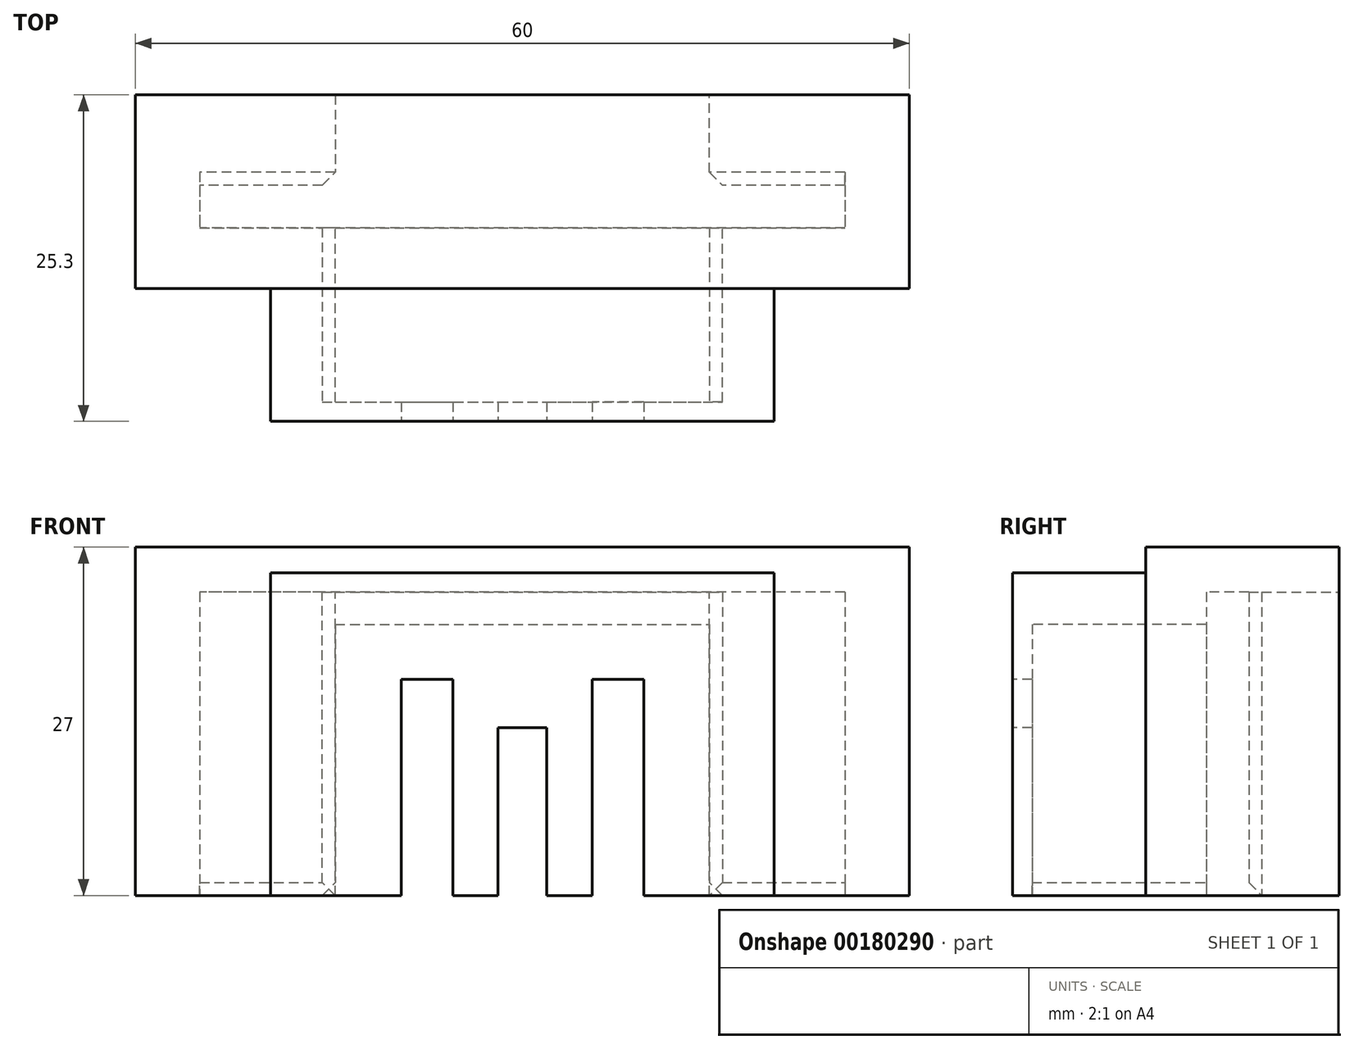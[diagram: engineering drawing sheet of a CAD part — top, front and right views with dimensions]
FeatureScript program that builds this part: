
annotation { "Feature Type Name" : "Feature", "Feature Type Description" : "" }
export const myFeature = defineFeature(function(context is Context, id is Id, definition is map)
    precondition{}
    {
        {
            var Q0;
            Q0=qCreatedBy(makeId("Front.planeOp"),FACE);
            var sketch = newSketch(context, id + "F0", { "sketchPlane" : qUnion([Q0])});
            skLineSegment(sketch, "E0", {"start": v(14.25, 0) * mm, "end": v(14.25, 21) * mm, "construction": true});
            skPoint(sketch, "E1.visualSharp", {"position": v(0, 0) * mm});
            skLineSegment(sketch, "E2.6", {"start": v(-0.25, 21) * mm, "end": v(28.75, 21) * mm});
            skLineSegment(sketch, "E3", {"start": v(-0.25, 21) * mm, "end": v(-0.25, 0) * mm});
            skLineSegment(sketch, "E4", {"start": v(28.75, 21) * mm, "end": v(28.75, 0) * mm});
            skLineSegment(sketch, "E5.0", {"start": v(-3.25, 23.75) * mm, "end": v(-3.25, 0) * mm});
            skLineSegment(sketch, "E5.4", {"start": v(-3.25, 23.75) * mm, "end": v(31.75, 23.75) * mm});
            skLineSegment(sketch, "E5.5", {"start": v(31.75, 23.75) * mm, "end": v(31.75, 0) * mm});
            skLineSegment(sketch, "E6", {"start": v(-3.25, 0) * mm, "end": v(-0.25, 0) * mm});
            skLineSegment(sketch, "E7", {"start": v(28.75, 0) * mm, "end": v(31.75, 0) * mm});
            skLineSegment(sketch, "E8", {"start": v(-0.25, 0) * mm, "end": v(28.75, 0) * mm, "construction": true});
            skSolve(sketch);
        }
        {
            var Q0;
            Q0=qSketchRegion(id+"F0",true);
            extrude(context, id + "F1", {"entities" : qUnion([Q0]), "oppositeDirection" : true, "depth" : 15.8 * mm});
        }
        {
            var Q0;
            Q0=makeQuery(id+"F1.opExtrude","CAP_FACE",FACE,{"disambiguationData":[OSD([sQuery(id+"F0.wireOp",EDGE,"E2.0"),sQuery(id+"F0.wireOp",EDGE,"E2.1"),sQuery(id+"F0.wireOp",EDGE,"E2.2"),sQuery(id+"F0.wireOp",EDGE,"E2.3"),sQuery(id+"F0.wireOp",EDGE,"E2.4"),sQuery(id+"F0.wireOp",EDGE,"E2.5"),sQuery(id+"F0.wireOp",EDGE,"E2.6"),sQuery(id+"F0.wireOp",EDGE,"E3"),sQuery(id+"F0.wireOp",EDGE,"E4"),sQuery(id+"F0.wireOp",EDGE,"E5.0"),sQuery(id+"F0.wireOp",EDGE,"E5.1"),sQuery(id+"F0.wireOp",EDGE,"E5.2"),sQuery(id+"F0.wireOp",EDGE,"E5.3"),sQuery(id+"F0.wireOp",EDGE,"E5.4"),sQuery(id+"F0.wireOp",EDGE,"E5.5"),sQuery(id+"F0.wireOp",EDGE,"E5.6"),sQuery(id+"F0.wireOp",EDGE,"E5.7"),sQuery(id+"F0.wireOp",EDGE,"E5.8"),sQuery(id+"F0.wireOp",EDGE,"E6"),sQuery(id+"F0.wireOp",EDGE,"E7")])],"isStart":true});
            var sketch = newSketch(context, id + "F2", { "sketchPlane" : qUnion([Q0])});
            skLineSegment(sketch, "E9", {"start": v(-0.25, 0) * mm, "end": v(4.85, 0) * mm});
            skLineSegment(sketch, "E10.0", {"start": v(23.65, 16.75) * mm, "end": v(23.65, 0) * mm});
            skLineSegment(sketch, "E10.2", {"start": v(19.65, 16.75) * mm, "end": v(19.65, 0) * mm});
            skLineSegment(sketch, "E11.0", {"start": v(4.85, 16.75) * mm, "end": v(4.85, 0) * mm});
            skLineSegment(sketch, "E11.2", {"start": v(8.85, 16.75) * mm, "end": v(8.85, 0) * mm});
            skLineSegment(sketch, "E12.0", {"start": v(16.15, 13) * mm, "end": v(16.15, 0) * mm});
            skLineSegment(sketch, "E12.2", {"start": v(12.35, 13) * mm, "end": v(12.35, 0) * mm});
            skLineSegment(sketch, "E13", {"start": v(8.85, 0) * mm, "end": v(12.35, 0) * mm});
            skLineSegment(sketch, "E14", {"start": v(16.15, 0) * mm, "end": v(19.65, 0) * mm});
            skLineSegment(sketch, "E15", {"start": v(23.65, 0) * mm, "end": v(28.75, 0) * mm});
            skLineSegment(sketch, "E16.0", {"start": v(4.85, 16.75) * mm, "end": v(8.85, 16.75) * mm});
            skLineSegment(sketch, "E17.0", {"start": v(12.35, 13) * mm, "end": v(16.15, 13) * mm});
            skLineSegment(sketch, "E18.0", {"start": v(23.65, 16.75) * mm, "end": v(19.65, 16.75) * mm});
            skLineSegment(sketch, "E19.0", {"start": v(28.75, 21) * mm, "end": v(28.75, 0) * mm});
            skLineSegment(sketch, "E19.4", {"start": v(-0.25, 21) * mm, "end": v(28.75, 21) * mm});
            skLineSegment(sketch, "E19.8", {"start": v(-0.25, 21) * mm, "end": v(-0.25, 0) * mm});
            skPoint(sketch, "E20.orphan", {"position": v(-3.25, 0) * mm});
            skPoint(sketch, "E21.orphan", {"position": v(31.75, 0) * mm});
            skLineSegment(sketch, "E22", {"start": v(14.25, 13) * mm, "end": v(14.25, 21) * mm, "construction": true});
            skSolve(sketch);
        }
        {
            var Q0;
            Q0=qSketchRegion(id+"F2",true);
            extrude(context, id + "F3", {"entities" : qUnion([Q0]), "operationType" : NewBodyOperationType.ADD, "oppositeDirection" : true, "depth" : 2 * mm});
        }
        {
            var Q0;
            Q0=makeQuery(id+"F1.opExtrude","CAP_FACE",FACE,{"disambiguationData":[OSD([sQuery(id+"F0.wireOp",EDGE,"E2.0"),sQuery(id+"F0.wireOp",EDGE,"E2.1"),sQuery(id+"F0.wireOp",EDGE,"E2.2"),sQuery(id+"F0.wireOp",EDGE,"E2.3"),sQuery(id+"F0.wireOp",EDGE,"E2.4"),sQuery(id+"F0.wireOp",EDGE,"E2.5"),sQuery(id+"F0.wireOp",EDGE,"E2.6"),sQuery(id+"F0.wireOp",EDGE,"E3"),sQuery(id+"F0.wireOp",EDGE,"E4"),sQuery(id+"F0.wireOp",EDGE,"E5.0"),sQuery(id+"F0.wireOp",EDGE,"E5.4"),sQuery(id+"F0.wireOp",EDGE,"E5.5"),sQuery(id+"F0.wireOp",EDGE,"E6"),sQuery(id+"F0.wireOp",EDGE,"E7")])],"isStart":false});
            var sketch = newSketch(context, id + "F4", { "sketchPlane" : qUnion([Q0])});
            skLineSegment(sketch, "E23", {"start": v(-39.25, 23.5) * mm, "end": v(10.75, 23.5) * mm});
            skLineSegment(sketch, "E24", {"start": v(-14.25, 21) * mm, "end": v(-14.25, 23.5) * mm, "construction": true});
            skLineSegment(sketch, "E25", {"start": v(10.75, 23.5) * mm, "end": v(10.75, 0) * mm});
            skLineSegment(sketch, "E26", {"start": v(-39.25, 23.5) * mm, "end": v(-39.25, 0) * mm});
            skLineSegment(sketch, "E27.bottom", {"start": v(-49.25, 0) * mm, "end": v(-39.25, 0) * mm});
            skLineSegment(sketch, "E27.top", {"start": v(-49.25, 35) * mm, "end": v(20.75, 35) * mm});
            skLineSegment(sketch, "E27.left", {"start": v(-49.25, 0) * mm, "end": v(-49.25, 35) * mm});
            skLineSegment(sketch, "E27.right", {"start": v(20.75, 0) * mm, "end": v(20.75, 35) * mm});
            skLineSegment(sketch, "E28.trimOffspring", {"start": v(10.75, 0) * mm, "end": v(20.75, 0) * mm});
            skSolve(sketch);
        }
        {
            var Q0;
            Q0=qSketchRegion(id+"F4",true);
            var Q1;
            {var subQ1=sQuery(id+"F4.wireOp",EDGE,"E25");Q1=makeQuery(id+"F4.imprint","IMPRINT",FACE,{"disambiguationData":[TD([[makeQuery(id+"F4.imprint","IMPRINT",EDGE,{"derivedFrom":subQ1}),1.0]])]});}
            extrude(context, id + "F5", {"entities" : qUnion([Q0, Q1]), "operationType" : NewBodyOperationType.ADD, "depth" : 10 * mm});
        }
        {
            var Q0;
            Q0=makeQuery(id+"F5.opExtrude","CAP_FACE",FACE,{"disambiguationData":[OSD([sQuery(id+"F4.wireOp",EDGE,"E23"),sQuery(id+"F4.wireOp",EDGE,"E25"),sQuery(id+"F4.wireOp",EDGE,"E26"),sQuery(id+"F4.wireOp",EDGE,"E27.bottom"),sQuery(id+"F4.wireOp",EDGE,"E27.top"),sQuery(id+"F4.wireOp",EDGE,"E27.left"),sQuery(id+"F4.wireOp",EDGE,"E27.right"),sQuery(id+"F4.wireOp",EDGE,"E28.trimOffspring")])],"isStart":false});
            var sketch = newSketch(context, id + "F6", { "sketchPlane" : qUnion([Q0])});
            skLineSegment(sketch, "E29.bottom", {"start": v(10.75, 23.5) * mm, "end": v(-39.25, 23.5) * mm});
            skLineSegment(sketch, "E29.top", {"start": v(10.75, 0) * mm, "end": v(-39.25, 0) * mm});
            skLineSegment(sketch, "E29.left", {"start": v(10.75, 23.5) * mm, "end": v(10.75, 0) * mm});
            skLineSegment(sketch, "E29.right", {"start": v(-39.25, 23.5) * mm, "end": v(-39.25, 0) * mm});
            skSolve(sketch);
        }
        {
            var Q0;
            Q0=makeQuery(id+"F6.imprint","IMPRINT",FACE,{"disambiguationData":[TD([[makeQuery(id+"F6.imprint","IMPRINT",EDGE,{"derivedFrom":sQuery(id+"F6.wireOp",EDGE,"E29.bottom")}),-1.0]])]});
            extrude(context, id + "F7", {"entities" : qUnion([Q0]), "operationType" : NewBodyOperationType.ADD, "oppositeDirection" : true, "depth" : 5 * mm});
        }
        {
            var Q0;
            Q0=makeQuery(id+"F5.opExtrude","CAP_FACE",FACE,{"disambiguationData":[OSD([sQuery(id+"F4.wireOp",EDGE,"E23"),sQuery(id+"F4.wireOp",EDGE,"E25"),sQuery(id+"F4.wireOp",EDGE,"E26"),sQuery(id+"F4.wireOp",EDGE,"E27.bottom"),sQuery(id+"F4.wireOp",EDGE,"E27.top"),sQuery(id+"F4.wireOp",EDGE,"E27.left"),sQuery(id+"F4.wireOp",EDGE,"E27.right"),sQuery(id+"F4.wireOp",EDGE,"E28.trimOffspring")])],"isStart":true});
            var sketch = newSketch(context, id + "F8", { "sketchPlane" : qUnion([Q0])});
            skLineSegment(sketch, "E30.bottom", {"start": v(-20.75, 35) * mm, "end": v(49.25, 35) * mm});
            skLineSegment(sketch, "E30.top", {"start": v(-20.75, 0) * mm, "end": v(-3.25, 0) * mm});
            skLineSegment(sketch, "E30.left", {"start": v(-20.75, 35) * mm, "end": v(-20.75, 0) * mm});
            skLineSegment(sketch, "E30.right", {"start": v(49.25, 35) * mm, "end": v(49.25, 0) * mm});
            skLineSegment(sketch, "E31", {"start": v(-3.25, 23.5) * mm, "end": v(-3.25, 0) * mm});
            skLineSegment(sketch, "E32", {"start": v(31.75, 23.5) * mm, "end": v(31.75, 0) * mm});
            skLineSegment(sketch, "E33", {"start": v(31.75, 23.75) * mm, "end": v(31.75, 23.5) * mm});
            skLineSegment(sketch, "E34", {"start": v(31.75, 23.75) * mm, "end": v(-3.25, 23.75) * mm});
            skLineSegment(sketch, "E35", {"start": v(-3.25, 23.75) * mm, "end": v(-3.25, 23.5) * mm});
            skLineSegment(sketch, "E36.trimOffspring", {"start": v(31.75, 0) * mm, "end": v(49.25, 0) * mm});
            skSolve(sketch);
        }
        {
            var Q0;
            Q0=qSketchRegion(id+"F8",true);
            extrude(context, id + "F9", {"entities" : qUnion([Q0]), "operationType" : NewBodyOperationType.ADD, "depth" : 15.8 * mm});
        }
        {
            var Q0;
            Q0=makeQuery(id+"FpBfA30VbHsMN9c_1.boolean.opBoolean","MERGE",FACE,{"derivedFrom":[makeQuery(id+"F9.boolean.opBoolean","MERGE",FACE,{"derivedFrom":[makeQuery(id+"F3.boolean.opBoolean","MERGE",FACE,{"derivedFrom":[makeQuery(id+"F1.opExtrude","SWEPT_FACE",FACE,{"disambiguationData":[OSD([sQuery(id+"F0.wireOp",EDGE,"E6")])]}),makeQuery(id+"F3.opExtrude","SWEPT_FACE",FACE,{"disambiguationData":[OSD([sQuery(id+"F2.wireOp",EDGE,"E9")])]})]}),makeQuery(id+"F3.boolean.opBoolean","MERGE",FACE,{"derivedFrom":[makeQuery(id+"F1.opExtrude","SWEPT_FACE",FACE,{"disambiguationData":[OSD([sQuery(id+"F0.wireOp",EDGE,"E7")])]}),makeQuery(id+"F3.opExtrude","SWEPT_FACE",FACE,{"disambiguationData":[OSD([sQuery(id+"F2.wireOp",EDGE,"E15")])]})]}),makeQuery(id+"F7.boolean.opBoolean","MERGE",FACE,{"derivedFrom":[makeQuery(id+"F5.opExtrude","SWEPT_FACE",FACE,{"disambiguationData":[OSD([sQuery(id+"F4.wireOp",EDGE,"E27.bottom")])]}),makeQuery(id+"F5.opExtrude","SWEPT_FACE",FACE,{"disambiguationData":[OSD([sQuery(id+"F4.wireOp",EDGE,"E28.trimOffspring")])]}),makeQuery(id+"F7.opExtrude","SWEPT_FACE",FACE,{"disambiguationData":[OSD([sQuery(id+"F6.wireOp",EDGE,"E29.top")])]})]}),makeQuery(id+"F9.opExtrude","SWEPT_FACE",FACE,{"disambiguationData":[OSD([sQuery(id+"F8.wireOp",EDGE,"E30.top")])]}),makeQuery(id+"F9.opExtrude","SWEPT_FACE",FACE,{"disambiguationData":[OSD([sQuery(id+"F8.wireOp",EDGE,"E36.trimOffspring")])]})]}),makeQuery(id+"FpBfA30VbHsMN9c_1.opExtrude","CAP_FACE",FACE,{"disambiguationData":[OSD([sQuery(id+"FI7q8aplz4JtIuN_1.wireOp",EDGE,"twPDsyeZ-qLfy-hEif-ozpC-9VHX31kboBlz.bottom"),sQuery(id+"FI7q8aplz4JtIuN_1.wireOp",EDGE,"twPDsyeZ-qLfy-hEif-ozpC-9VHX31kboBlz.top"),sQuery(id+"FI7q8aplz4JtIuN_1.wireOp",EDGE,"twPDsyeZ-qLfy-hEif-ozpC-9VHX31kboBlz.left"),sQuery(id+"FI7q8aplz4JtIuN_1.wireOp",EDGE,"twPDsyeZ-qLfy-hEif-ozpC-9VHX31kboBlz.right")])],"isStart":true}),makeQuery(id+"FpBfA30VbHsMN9c_1.opExtrude","CAP_FACE",FACE,{"disambiguationData":[OSD([sQuery(id+"FI7q8aplz4JtIuN_1.wireOp",EDGE,"suuiNPFj-Pw92-5tJ3-mqHD-LNdsG8Y2vCTz.bottom"),sQuery(id+"FI7q8aplz4JtIuN_1.wireOp",EDGE,"suuiNPFj-Pw92-5tJ3-mqHD-LNdsG8Y2vCTz.top"),sQuery(id+"FI7q8aplz4JtIuN_1.wireOp",EDGE,"suuiNPFj-Pw92-5tJ3-mqHD-LNdsG8Y2vCTz.left"),sQuery(id+"FI7q8aplz4JtIuN_1.wireOp",EDGE,"suuiNPFj-Pw92-5tJ3-mqHD-LNdsG8Y2vCTz.right")])],"isStart":true})]});
            var sketch = newSketch(context, id + "F10", { "sketchPlane" : qUnion([Q0])});
            skLineSegment(sketch, "E37", {"start": v(-20.75, 0) * mm, "end": v(-5.25, 0) * mm});
            skLineSegment(sketch, "E38", {"start": v(33.75, 0) * mm, "end": v(49.25, 0) * mm});
            skLineSegment(sketch, "E39", {"start": v(-5.25, 0) * mm, "end": v(-5.25, -10.8) * mm});
            skLineSegment(sketch, "E40", {"start": v(-5.25, -10.8) * mm, "end": v(-15.75, -10.8) * mm});
            skLineSegment(sketch, "E41", {"start": v(-15.75, -10.8) * mm, "end": v(-15.75, -25.8) * mm});
            skLineSegment(sketch, "E42", {"start": v(-20.75, 0) * mm, "end": v(-20.75, -25.8) * mm});
            skLineSegment(sketch, "E43", {"start": v(-20.75, -25.8) * mm, "end": v(-15.75, -25.8) * mm});
            skLineSegment(sketch, "E44", {"start": v(14.25, -25.8) * mm, "end": v(14.25, 0) * mm, "construction": true});
            skPoint(sketch, "E44.endSnap0", {"position": v(14.25, -20.8) * mm});
            skLineSegment(sketch, "E45.MirrorCS", {"start": v(33.75, -10.8) * mm, "end": v(44.25, -10.8) * mm});
            skLineSegment(sketch, "E46.MirrorCS", {"start": v(49.25, -25.8) * mm, "end": v(44.25, -25.8) * mm});
            skLineSegment(sketch, "E47.MirrorCS", {"start": v(44.25, -10.8) * mm, "end": v(44.25, -25.8) * mm});
            skLineSegment(sketch, "E48.MirrorCS", {"start": v(33.75, 0) * mm, "end": v(33.75, -10.8) * mm});
            skLineSegment(sketch, "E49.MirrorCS", {"start": v(49.25, 0) * mm, "end": v(33.75, 0) * mm});
            skLineSegment(sketch, "E50.MirrorCS", {"start": v(49.25, 0) * mm, "end": v(49.25, -25.8) * mm});
            skSolve(sketch);
        }
        {
            var Q0;
            Q0=makeQuery(id+"F10.imprint","IMPRINT",FACE,{"disambiguationData":[TD([[makeQuery(id+"F10.imprint","IMPRINT",EDGE,{"derivedFrom":sQuery(id+"F10.wireOp",EDGE,"E45.MirrorCS")}),1.0]])]});
            var Q1;
            Q1=makeQuery(id+"F10.imprint","IMPRINT",FACE,{"disambiguationData":[TD([[makeQuery(id+"F10.imprint","IMPRINT",EDGE,{"derivedFrom":sQuery(id+"F10.wireOp",EDGE,"E37")}),-1.0]])]});
            extrude(context, id + "F11", {"entities" : qUnion([Q0, Q1]), "operationType" : NewBodyOperationType.REMOVE, "endBound" : BoundingType.THROUGH_ALL, "oppositeDirection" : true, "depth" : 25 * mm});
        }
        {
            var Q0;
            Q0=makeQuery(id+"F9.boolean.opBoolean","MERGE",FACE,{"derivedFrom":[makeQuery(id+"F5.opExtrude","SWEPT_FACE",FACE,{"disambiguationData":[OSD([sQuery(id+"F4.wireOp",EDGE,"E27.top")])]}),makeQuery(id+"F9.opExtrude","SWEPT_FACE",FACE,{"disambiguationData":[OSD([sQuery(id+"F8.wireOp",EDGE,"E30.bottom")])]})]});
            var sketch = newSketch(context, id + "F12", { "sketchPlane" : qUnion([Q0])});
            skLineSegment(sketch, "E51.bottom", {"start": v(33.75, 0) * mm, "end": v(-5.25, 0) * mm});
            skLineSegment(sketch, "E51.top", {"start": v(33.75, 10.8) * mm, "end": v(-5.25, 10.8) * mm});
            skLineSegment(sketch, "E51.left", {"start": v(33.75, 0) * mm, "end": v(33.75, 10.8) * mm});
            skLineSegment(sketch, "E51.right", {"start": v(-5.25, 0) * mm, "end": v(-5.25, 10.8) * mm});
            skSolve(sketch);
        }
        {
            var Q0;
            Q0=qSketchRegion(id+"F12",true);
            var Q1;
            Q1=makeQuery(id+"F1.opExtrude","SWEPT_FACE",FACE,{"disambiguationData":[OSD([sQuery(id+"F0.wireOp",EDGE,"E2.6")])]});
            extrude(context, id + "F13", {"entities" : qUnion([Q0, Q1]), "operationType" : NewBodyOperationType.REMOVE, "oppositeDirection" : true, "depth" : 10 * mm});
        }
        {
            var Q0;
            Q0=makeQuery(id+"F9.boolean.opBoolean","MERGE",FACE,{"derivedFrom":[makeQuery(id+"F5.opExtrude","SWEPT_FACE",FACE,{"disambiguationData":[OSD([sQuery(id+"F4.wireOp",EDGE,"E27.top")])]}),makeQuery(id+"F9.opExtrude","SWEPT_FACE",FACE,{"disambiguationData":[OSD([sQuery(id+"F8.wireOp",EDGE,"E30.bottom")])]})]});
            var sketch = newSketch(context, id + "F14", { "sketchPlane" : qUnion([Q0])});
            skLineSegment(sketch, "E52.bottom", {"start": v(44.25, 10.8) * mm, "end": v(-15.75, 10.8) * mm});
            skLineSegment(sketch, "E52.top", {"start": v(44.25, 25.8) * mm, "end": v(-15.75, 25.8) * mm});
            skLineSegment(sketch, "E52.left", {"start": v(44.25, 10.8) * mm, "end": v(44.25, 25.8) * mm});
            skLineSegment(sketch, "E52.right", {"start": v(-15.75, 10.8) * mm, "end": v(-15.75, 25.8) * mm});
            skSolve(sketch);
        }
        {
            var Q0;
            Q0=qSketchRegion(id+"F14",true);
            extrude(context, id + "F15", {"entities" : qUnion([Q0]), "operationType" : NewBodyOperationType.REMOVE, "oppositeDirection" : true, "depth" : 8 * mm});
        }
        {
            var Q0;
            Q0=makeQuery(id+"F7.opExtrude","CAP_FACE",FACE,{"disambiguationData":[OSD([sQuery(id+"F6.wireOp",EDGE,"E29.bottom"),sQuery(id+"F6.wireOp",EDGE,"E29.top"),sQuery(id+"F6.wireOp",EDGE,"E29.left"),sQuery(id+"F6.wireOp",EDGE,"E29.right")])],"isStart":false});
            extrude(context, id + "F16", {"entities" : qUnion([Q0]), "operationType" : NewBodyOperationType.REMOVE, "oppositeDirection" : true, "depth" : 0.5 * mm});
        }
        {
            var Q0;
            Q0=makeQuery(id+"F9.boolean.opBoolean","MERGE",FACE,{"derivedFrom":[makeQuery(id+"F3.boolean.opBoolean","MERGE",FACE,{"derivedFrom":[makeQuery(id+"F1.opExtrude","SWEPT_FACE",FACE,{"disambiguationData":[OSD([sQuery(id+"F0.wireOp",EDGE,"E6")])]}),makeQuery(id+"F3.opExtrude","SWEPT_FACE",FACE,{"disambiguationData":[OSD([sQuery(id+"F2.wireOp",EDGE,"E9")])]})]}),makeQuery(id+"F3.boolean.opBoolean","MERGE",FACE,{"derivedFrom":[makeQuery(id+"F1.opExtrude","SWEPT_FACE",FACE,{"disambiguationData":[OSD([sQuery(id+"F0.wireOp",EDGE,"E7")])]}),makeQuery(id+"F3.opExtrude","SWEPT_FACE",FACE,{"disambiguationData":[OSD([sQuery(id+"F2.wireOp",EDGE,"E15")])]})]}),makeQuery(id+"F7.boolean.opBoolean","MERGE",FACE,{"derivedFrom":[makeQuery(id+"F5.opExtrude","SWEPT_FACE",FACE,{"disambiguationData":[OSD([sQuery(id+"F4.wireOp",EDGE,"E27.bottom")])]}),makeQuery(id+"F5.opExtrude","SWEPT_FACE",FACE,{"disambiguationData":[OSD([sQuery(id+"F4.wireOp",EDGE,"E28.trimOffspring")])]}),makeQuery(id+"F7.opExtrude","SWEPT_FACE",FACE,{"disambiguationData":[OSD([sQuery(id+"F6.wireOp",EDGE,"E29.top")])]})]}),makeQuery(id+"F9.opExtrude","SWEPT_FACE",FACE,{"disambiguationData":[OSD([sQuery(id+"F8.wireOp",EDGE,"E30.top")])]}),makeQuery(id+"F9.opExtrude","SWEPT_FACE",FACE,{"disambiguationData":[OSD([sQuery(id+"F8.wireOp",EDGE,"E36.trimOffspring")])]})]});
            var sketch = newSketch(context, id + "F17", { "sketchPlane" : qUnion([Q0])});
            skLineSegment(sketch, "E53.bottom", {"start": v(-10.75, -21.3) * mm, "end": v(-0.25, -21.3) * mm});
            skLineSegment(sketch, "E53.top", {"start": v(-10.75, -18.8) * mm, "end": v(-0.25, -18.8) * mm});
            skLineSegment(sketch, "E53.left", {"start": v(-10.75, -21.3) * mm, "end": v(-10.75, -18.8) * mm});
            skLineSegment(sketch, "E53.right", {"start": v(-0.25, -21.3) * mm, "end": v(-0.25, -18.8) * mm});
            skLineSegment(sketch, "E54.bottom", {"start": v(28.75, -18.8) * mm, "end": v(39.25, -18.8) * mm});
            skLineSegment(sketch, "E54.top", {"start": v(28.75, -21.3) * mm, "end": v(39.25, -21.3) * mm});
            skLineSegment(sketch, "E54.left", {"start": v(28.75, -18.8) * mm, "end": v(28.75, -21.3) * mm});
            skLineSegment(sketch, "E54.right", {"start": v(39.25, -18.8) * mm, "end": v(39.25, -21.3) * mm});
            skSolve(sketch);
        }
        {
            var Q0;
            Q0 = qSketchRegion(id + "F17", true);
            extrude(context, id + "F18", {"entities" : qUnion([Q0]), "operationType" : NewBodyOperationType.ADD, "oppositeDirection" : true, "depth" : 24 * mm});
        }
        {
            var Q0;
            Q0=makeQuery(id+"F16.boolean.opBoolean","COPY",FACE,{"derivedFrom":makeQuery(id+"F16.opExtrude","CAP_FACE",FACE,{"disambiguationData":[OSD([sQuery(id+"F6.wireOp",EDGE,"E29.bottom"),sQuery(id+"F6.wireOp",EDGE,"E29.top"),sQuery(id+"F6.wireOp",EDGE,"E29.left"),sQuery(id+"F6.wireOp",EDGE,"E29.right")])],"isStart":false})});
            extrude(context, id + "F19", {"entities" : qUnion([Q0]), "operationType" : NewBodyOperationType.REMOVE, "oppositeDirection" : true, "depth" : 25 * mm});
        }
        {
            var Q0;
            Q0=makeQuery(id+"F9.boolean.opBoolean","MERGE",FACE,{"derivedFrom":[makeQuery(id+"F1.opExtrude","CAP_FACE",FACE,{"disambiguationData":[OSD([sQuery(id+"F0.wireOp",EDGE,"E2.6"),sQuery(id+"F0.wireOp",EDGE,"E3"),sQuery(id+"F0.wireOp",EDGE,"E4"),sQuery(id+"F0.wireOp",EDGE,"E5.0"),sQuery(id+"F0.wireOp",EDGE,"E5.4"),sQuery(id+"F0.wireOp",EDGE,"E5.5"),sQuery(id+"F0.wireOp",EDGE,"E6"),sQuery(id+"F0.wireOp",EDGE,"E7")])],"isStart":false}),makeQuery(id+"F9.opExtrude","CAP_FACE",FACE,{"disambiguationData":[OSD([sQuery(id+"F8.wireOp",EDGE,"E30.bottom"),sQuery(id+"F8.wireOp",EDGE,"E30.top"),sQuery(id+"F8.wireOp",EDGE,"E30.left"),sQuery(id+"F8.wireOp",EDGE,"E30.right"),sQuery(id+"F8.wireOp",EDGE,"E31"),sQuery(id+"F8.wireOp",EDGE,"E32"),sQuery(id+"F8.wireOp",EDGE,"E33"),sQuery(id+"F8.wireOp",EDGE,"E34"),sQuery(id+"F8.wireOp",EDGE,"E35"),sQuery(id+"F8.wireOp",EDGE,"E36.trimOffspring")])],"isStart":true})]});
            extrude(context, id + "F20", {"entities" : qUnion([Q0]), "operationType" : NewBodyOperationType.REMOVE, "oppositeDirection" : true, "depth" : 0.3 * mm});
        }
        {
            var Q0;
            Q0=makeQuery(id+"F1.opExtrude","SWEPT_EDGE",EDGE,{"disambiguationData":[OSD([sQuery(id+"F0.wireOp",EDGE,"E3"),sQuery(id+"F0.wireOp",EDGE,"E6")])]});
            var Q1;
            Q1=makeQuery(id+"F9.boolean.opBoolean","MERGE",EDGE,{"derivedFrom":[makeQuery(id+"F1.opExtrude","CAP_EDGE",EDGE,{"disambiguationData":[OSD([sQuery(id+"F0.wireOp",EDGE,"E6")])],"isStart":false}),makeQuery(id+"F9.opExtrude","CAP_EDGE",EDGE,{"disambiguationData":[OSD([sQuery(id+"F8.wireOp",EDGE,"E30.top")])],"isStart":true})]});
            var Q2;
            {var subQ0=sQuery(id+"F4.wireOp",EDGE,"E28.trimOffspring");Q2=makeQuery(id+"F16.boolean.opBoolean","MERGE",EDGE,{"derivedFrom":[makeQuery(id+"F5.opExtrude","SWEPT_EDGE",EDGE,{"disambiguationData":[OSD([sQuery(id+"F4.wireOp",EDGE,"E25"),subQ0])]}),makeQuery(id+"F16.opExtrude","SWEPT_EDGE",EDGE,{"disambiguationData":[OSD([subQ0,sQuery(id+"F6.wireOp",EDGE,"E29.top"),sQuery(id+"F6.wireOp",EDGE,"E29.left")])]})]});}
            var Q3;
            Q3=makeQuery(id+"F16.boolean.opBoolean","COPY",EDGE,{"derivedFrom":makeQuery(id+"F16.opExtrude","CAP_EDGE",EDGE,{"disambiguationData":[OSD([sQuery(id+"F6.wireOp",EDGE,"E29.top")])],"isStart":false})});
            var Q4;
            {var subQ0=sQuery(id+"F4.wireOp",EDGE,"E27.bottom");Q4=makeQuery(id+"F16.boolean.opBoolean","MERGE",EDGE,{"derivedFrom":[makeQuery(id+"F5.opExtrude","SWEPT_EDGE",EDGE,{"disambiguationData":[OSD([sQuery(id+"F4.wireOp",EDGE,"E26"),subQ0])]}),makeQuery(id+"F16.opExtrude","SWEPT_EDGE",EDGE,{"disambiguationData":[OSD([subQ0,sQuery(id+"F6.wireOp",EDGE,"E29.top"),sQuery(id+"F6.wireOp",EDGE,"E29.right")])]})]});}
            var Q5;
            Q5=makeQuery(id+"F9.boolean.opBoolean","MERGE",EDGE,{"derivedFrom":[makeQuery(id+"F1.opExtrude","CAP_EDGE",EDGE,{"disambiguationData":[OSD([sQuery(id+"F0.wireOp",EDGE,"E7")])],"isStart":false}),makeQuery(id+"F9.opExtrude","CAP_EDGE",EDGE,{"disambiguationData":[OSD([sQuery(id+"F8.wireOp",EDGE,"E36.trimOffspring")])],"isStart":true})]});
            var Q6;
            Q6=makeQuery(id+"F1.opExtrude","SWEPT_EDGE",EDGE,{"disambiguationData":[OSD([sQuery(id+"F0.wireOp",EDGE,"E4"),sQuery(id+"F0.wireOp",EDGE,"E7")])]});
            var Q7;
            Q7=makeQuery(id+"F1.opExtrude","CAP_EDGE",EDGE,{"disambiguationData":[OSD([sQuery(id+"F0.wireOp",EDGE,"E4")])],"isStart":false});
            var Q8;
            Q8=makeQuery(id+"F1.opExtrude","CAP_EDGE",EDGE,{"disambiguationData":[OSD([sQuery(id+"F0.wireOp",EDGE,"E3")])],"isStart":false});
            var Q9;
            Q9=makeQuery(id+"F18.opExtrude","CAP_EDGE",EDGE,{"disambiguationData":[OSD([sQuery(id+"F17.wireOp",EDGE,"E54.bottom")])],"isStart":true});
            var Q10;
            Q10=makeQuery(id+"F18.opExtrude","CAP_EDGE",EDGE,{"disambiguationData":[OSD([sQuery(id+"F17.wireOp",EDGE,"E53.top")])],"isStart":true});
            var Q11;
            Q11=makeQuery(id+"F18.opExtrude","SWEPT_EDGE",EDGE,{"disambiguationData":[OSD([sQuery(id+"F17.wireOp",EDGE,"E53.top"),sQuery(id+"F17.wireOp",EDGE,"E53.right")])]});
            var Q12;
            Q12=makeQuery(id+"F18.opExtrude","SWEPT_EDGE",EDGE,{"disambiguationData":[OSD([sQuery(id+"F17.wireOp",EDGE,"E54.bottom"),sQuery(id+"F17.wireOp",EDGE,"E54.left")])]});
            chamfer(context, id + "F21", {"entities" : qUnion([Q0, Q1, Q2, Q3, Q4, Q5, Q6, Q7, Q8, Q9, Q10, Q11, Q12]), "width" : 1 * mm, "tangentPropagation" : true});
        }
        {
            var Q0;
            Q0=makeQuery(id+"F9.boolean.opBoolean","MERGE",FACE,{"derivedFrom":[makeQuery(id+"F3.boolean.opBoolean","MERGE",FACE,{"derivedFrom":[makeQuery(id+"F1.opExtrude","CAP_FACE",FACE,{"disambiguationData":[OSD([sQuery(id+"F0.wireOp",EDGE,"E2.6"),sQuery(id+"F0.wireOp",EDGE,"E3"),sQuery(id+"F0.wireOp",EDGE,"E4"),sQuery(id+"F0.wireOp",EDGE,"E5.0"),sQuery(id+"F0.wireOp",EDGE,"E5.4"),sQuery(id+"F0.wireOp",EDGE,"E5.5"),sQuery(id+"F0.wireOp",EDGE,"E6"),sQuery(id+"F0.wireOp",EDGE,"E7")])],"isStart":true}),makeQuery(id+"F3.opExtrude","CAP_FACE",FACE,{"disambiguationData":[OSD([sQuery(id+"F2.wireOp",EDGE,"E10.0"),sQuery(id+"F2.wireOp",EDGE,"E10.2"),sQuery(id+"F2.wireOp",EDGE,"E11.0"),sQuery(id+"F2.wireOp",EDGE,"E11.2"),sQuery(id+"F2.wireOp",EDGE,"E12.0"),sQuery(id+"F2.wireOp",EDGE,"E12.2"),sQuery(id+"F2.wireOp",EDGE,"E9"),sQuery(id+"F2.wireOp",EDGE,"E13"),sQuery(id+"F2.wireOp",EDGE,"E15"),sQuery(id+"F2.wireOp",EDGE,"E14"),sQuery(id+"F2.wireOp",EDGE,"E16.0"),sQuery(id+"F2.wireOp",EDGE,"E17.0"),sQuery(id+"F2.wireOp",EDGE,"E18.0"),sQuery(id+"F2.wireOp",EDGE,"E19.0"),sQuery(id+"F2.wireOp",EDGE,"E19.4"),sQuery(id+"F2.wireOp",EDGE,"E19.8")])],"isStart":true})]}),makeQuery(id+"F9.opExtrude","CAP_FACE",FACE,{"disambiguationData":[OSD([sQuery(id+"F8.wireOp",EDGE,"E30.bottom"),sQuery(id+"F8.wireOp",EDGE,"E30.top"),sQuery(id+"F8.wireOp",EDGE,"E30.left"),sQuery(id+"F8.wireOp",EDGE,"E30.right"),sQuery(id+"F8.wireOp",EDGE,"E31"),sQuery(id+"F8.wireOp",EDGE,"E32"),sQuery(id+"F8.wireOp",EDGE,"E33"),sQuery(id+"F8.wireOp",EDGE,"E34"),sQuery(id+"F8.wireOp",EDGE,"E35"),sQuery(id+"F8.wireOp",EDGE,"E36.trimOffspring")])],"isStart":false})]});
            extrude(context, id + "F22", {"entities" : qUnion([Q0]), "operationType" : NewBodyOperationType.REMOVE, "oppositeDirection" : true, "depth" : 0.5 * mm});
        }
    });
